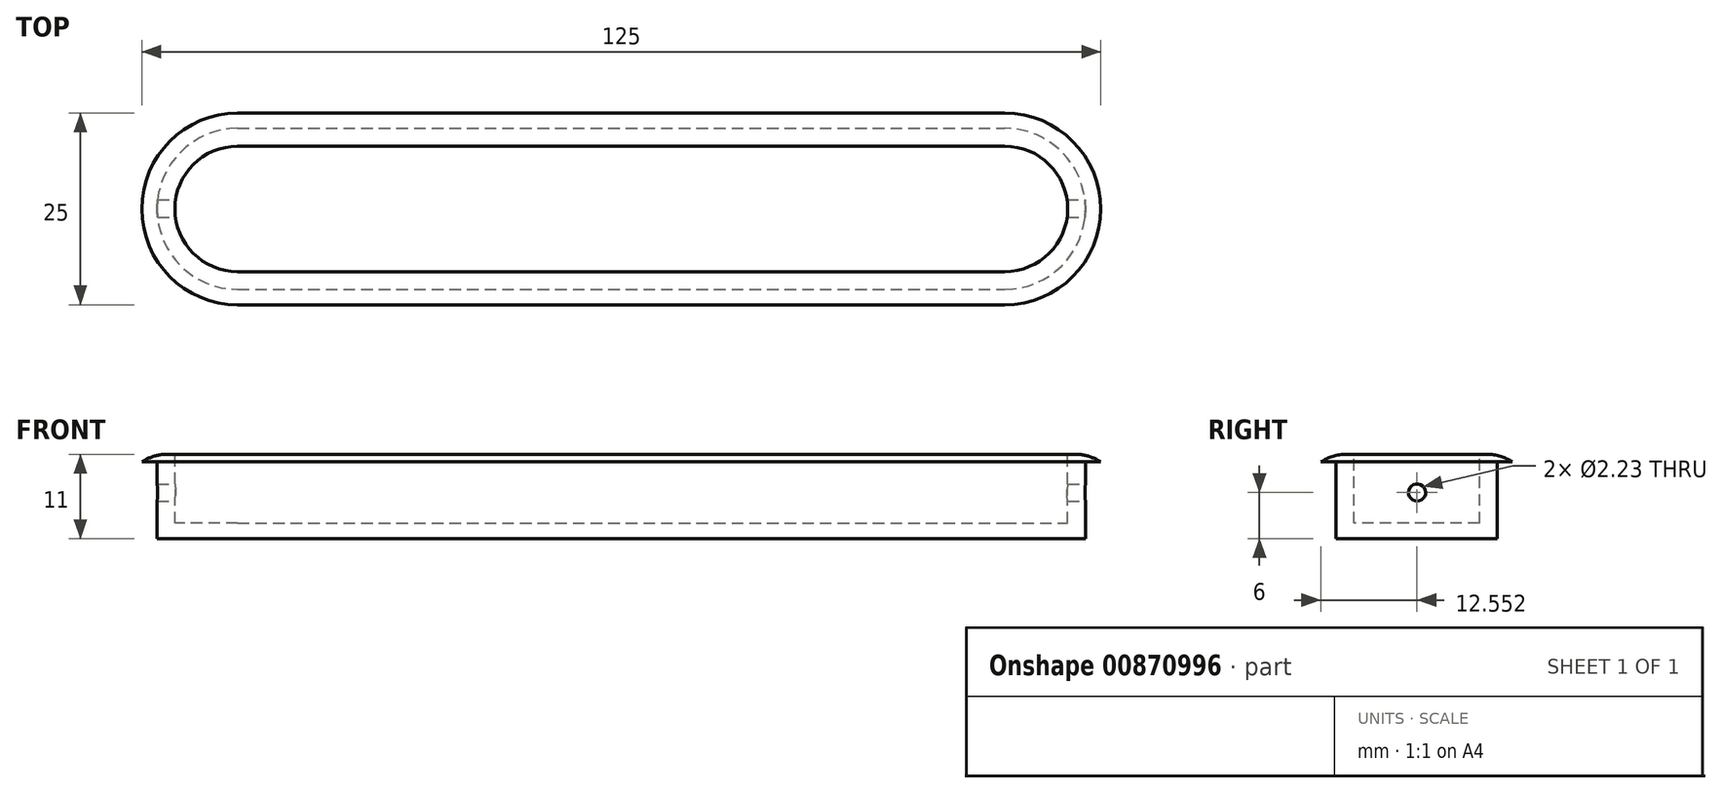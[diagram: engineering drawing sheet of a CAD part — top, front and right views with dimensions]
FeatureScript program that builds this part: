
annotation { "Feature Type Name" : "Feature", "Feature Type Description" : "" }
export const myFeature = defineFeature(function(context is Context, id is Id, definition is map)
    precondition{}
    {
        {
            var Q0;
            Q0=qCreatedBy(makeId("Top.planeOp"),FACE);
            var sketch = newSketch(context, id + "F0", { "sketchPlane" : qUnion([Q0])});
            skLineSegment(sketch, "E0.bottom", {"start": v(-51.35, 4.76) * mm, "end": v(48.65, 4.76) * mm});
            skLineSegment(sketch, "E0.top", {"start": v(-51.35, -16.24) * mm, "end": v(48.65, -16.24) * mm});
            skArc(sketch, "E1", {"start": v(-51.35, 4.76) * mm, "mid": v(-61.85, -5.74) * mm, "end": v(-51.35, -16.24) * mm});
            skArc(sketch, "E2", {"start": v(48.65, -16.24) * mm, "mid": v(59.15, -5.74) * mm, "end": v(48.65, 4.76) * mm});
            skSolve(sketch);
        }
        {
            var Q0;
            Q0 = qSketchRegion(id + "F0", true);
            extrude(context, id + "F1", {"entities" : qUnion([Q0]), "depth" : 10 * mm, "offsetDistance" : 25 * mm});
        }
        {
            var Q0;
            Q0=makeQuery(id+"F1.opExtrude","CAP_FACE",FACE,{"disambiguationData":[OSD([sQuery(id+"F0.wireOp",EDGE,"E0.bottom"),sQuery(id+"F0.wireOp",EDGE,"E0.top"),sQuery(id+"F0.wireOp",EDGE,"E1"),sQuery(id+"F0.wireOp",EDGE,"E2")])],"isStart":false});
            var sketch = newSketch(context, id + "F2", { "sketchPlane" : qUnion([Q0])});
            skLineSegment(sketch, "E3", {"start": v(-51.35, 6.76) * mm, "end": v(48.65, 6.76) * mm});
            skLineSegment(sketch, "E4", {"start": v(-51.35, -18.24) * mm, "end": v(48.65, -18.24) * mm});
            skArc(sketch, "E5", {"start": v(-51.35, 6.76) * mm, "mid": v(-63.85, -5.74) * mm, "end": v(-51.35, -18.24) * mm});
            skArc(sketch, "E6", {"start": v(48.65, -18.24) * mm, "mid": v(61.15, -5.74) * mm, "end": v(48.65, 6.76) * mm});
            skPoint(sketch, "E7.start.orphan", {"position": v(-51.35, -16.24) * mm});
            skPoint(sketch, "E8.orphan", {"position": v(-51.35, 4.76) * mm});
            skSolve(sketch);
        }
        {
            var Q0;
            Q0=makeQuery(id+"F2.imprint","IMPRINT",FACE,{"disambiguationData":[TD([[makeQuery(id+"F2.imprint","IMPRINT",EDGE,{"derivedFrom":sQuery(id+"F2.wireOp",EDGE,"E3")}),-1.0]])]});
            var Q1;
            Q1=makeQuery(id+"F2.imprint","IMPRINT",FACE,{"disambiguationData":[TD([[makeQuery(id+"F2.imprint","IMPRINT",EDGE,{"derivedFrom":makeQuery(id+"F1.opExtrude","CAP_EDGE",EDGE,{"disambiguationData":[OSD([sQuery(id+"F0.wireOp",EDGE,"E0.bottom")])],"isStart":false})}),-1.0]])]});
            extrude(context, id + "F3", {"entities" : qUnion([Q0, Q1]), "operationType" : NewBodyOperationType.ADD, "depth" : 1 * mm, "offsetDistance" : 25 * mm});
        }
        {
            var Q0;
            Q0=makeQuery(id+"F3.opExtrude","CAP_EDGE",EDGE,{"disambiguationData":[OSD([sQuery(id+"F2.wireOp",EDGE,"E3")])],"isStart":false});
            var Q1;
            Q1=makeQuery(id+"F3.opExtrude","CAP_EDGE",EDGE,{"disambiguationData":[OSD([sQuery(id+"F2.wireOp",EDGE,"E6")])],"isStart":false});
            var Q2;
            Q2=makeQuery(id+"F3.opExtrude","CAP_EDGE",EDGE,{"disambiguationData":[OSD([sQuery(id+"F2.wireOp",EDGE,"E4")])],"isStart":false});
            var Q3;
            Q3=makeQuery(id+"F3.opExtrude","CAP_EDGE",EDGE,{"disambiguationData":[OSD([sQuery(id+"F2.wireOp",EDGE,"E5")])],"isStart":false});
            fillet(context, id + "F4", {"entities" : qUnion([Q0, Q1, Q2, Q3]), "tangentPropagation" : true, "radius" : 6 * mm, "defaultsChanged" : true, "vertexSettings" : [], "allowEdgeOverflow" : false});
        }
        {
            var Q0;
            Q0=makeQuery(id+"F3.opExtrude","CAP_FACE",FACE,{"disambiguationData":[OSD([sQuery(id+"F2.wireOp",EDGE,"E3"),sQuery(id+"F2.wireOp",EDGE,"E4"),sQuery(id+"F2.wireOp",EDGE,"E5"),sQuery(id+"F2.wireOp",EDGE,"E6")])],"isStart":false});
            var sketch = newSketch(context, id + "F5", { "sketchPlane" : qUnion([Q0])});
            skLineSegment(sketch, "E9.bottom", {"start": v(-51.35, 2.44) * mm, "end": v(48.65, 2.44) * mm});
            skLineSegment(sketch, "E9.top", {"start": v(-51.35, -13.92) * mm, "end": v(48.65, -13.92) * mm});
            skArc(sketch, "E10", {"start": v(-51.35, 2.44) * mm, "mid": v(-59.53, -5.74) * mm, "end": v(-51.35, -13.92) * mm});
            skArc(sketch, "E11", {"start": v(48.65, -13.92) * mm, "mid": v(56.83, -5.74) * mm, "end": v(48.65, 2.44) * mm});
            skSolve(sketch);
        }
        {
            var Q0;
            Q0=makeQuery(id+"F5.imprint","IMPRINT",FACE,{"disambiguationData":[TD([[makeQuery(id+"F5.imprint","IMPRINT",EDGE,{"derivedFrom":sQuery(id+"F5.wireOp",EDGE,"E9.bottom")}),-1.0]])]});
            extrude(context, id + "F6", {"entities" : qUnion([Q0]), "operationType" : NewBodyOperationType.REMOVE, "oppositeDirection" : true, "depth" : 9 * mm, "offsetDistance" : 25 * mm});
        }
        {
            var Q0;
            Q0=qCreatedBy(makeId("Right.planeOp"),FACE);
            var sketch = newSketch(context, id + "F7", { "sketchPlane" : qUnion([Q0])});
            skCircle(sketch, "E12", {"center": v(-5.69, 6) * mm, "radius": 1.12 * mm});
            skSolve(sketch);
        }
        {
            var Q0;
            Q0=makeQuery(id+"F7.imprint","IMPRINT",FACE,{"disambiguationData":[TD([[makeQuery(id+"F7.imprint","IMPRINT",EDGE,{"derivedFrom":sQuery(id+"F7.wireOp",EDGE,"E12")}),1.0]])]});
            extrude(context, id + "F8", {"entities" : qUnion([Q0]), "operationType" : NewBodyOperationType.REMOVE, "endBound" : BoundingType.SYMMETRIC, "oppositeDirection" : true, "depth" : 200 * mm, "offsetDistance" : 25 * mm});
        }
    });
